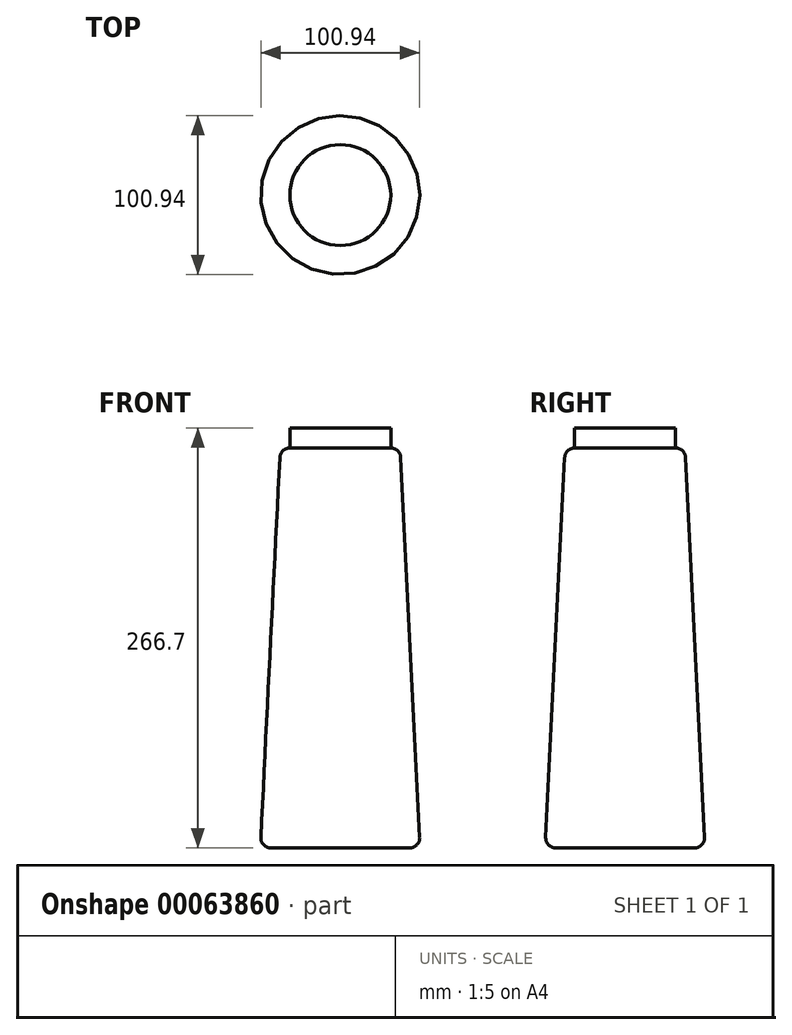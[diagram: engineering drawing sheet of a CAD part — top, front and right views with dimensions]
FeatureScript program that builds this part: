
annotation { "Feature Type Name" : "Feature", "Feature Type Description" : "" }
export const myFeature = defineFeature(function(context is Context, id is Id, definition is map)
    precondition{}
    {
        {
            var Q0;
            Q0=qCreatedBy(makeId("Top.planeOp"),FACE);
            var sketch = newSketch(context, id + "F0", { "sketchPlane" : qUnion([Q0])});
            skCircle(sketch, "E0", {"center": v(0, 0) * mm, "radius": 50.8 * mm});
            skSolve(sketch);
        }
        {
            var Q0;
            Q0=qCreatedBy(makeId("Top.planeOp"),FACE);
            cPlane(context, id + "F1", {"entities" : qUnion([Q0]), "cplaneType" : CPlaneType.OFFSET, "offset" : 254 * mm, "width" : 152.4 * mm, "height" : 152.4 * mm});
        }
        {
            var Q0;
            Q0=qCreatedBy(id+"F1.planeOp",FACE);
            var sketch = newSketch(context, id + "F2", { "sketchPlane" : qUnion([Q0])});
            skCircle(sketch, "E1", {"center": v(0, 0) * mm, "radius": 38.1 * mm});
            skSolve(sketch);
        }
        {
            var Q0;
            Q0=makeQuery(id+"F0.imprint","IMPRINT",FACE,{"disambiguationData":[TD([[makeQuery(id+"F0.imprint","IMPRINT",EDGE,{"derivedFrom":sQuery(id+"F0.wireOp",EDGE,"E0")}),1.0]])]});
            var Q1;
            Q1=makeQuery(id+"F2.imprint","IMPRINT",FACE,{"disambiguationData":[TD([[makeQuery(id+"F2.imprint","IMPRINT",EDGE,{"derivedFrom":sQuery(id+"F2.wireOp",EDGE,"E1")}),1.0]])]});
            loft(context, id + "F3", {"sheetProfilesArray" : [{ "sheetProfileEntities" : qUnion([Q0]) }, { "sheetProfileEntities" : qUnion([Q1]) }]});
        }
        {
            var Q0;
            Q0=makeQuery(id+"F3.opLoft","SWEPT_FACE",FACE,{"disambiguationData":[OSD([sQuery(id+"F0.wireOp",EDGE,"E0"),sQuery(id+"F2.wireOp",EDGE,"E1")])]});
            fillet(context, id + "F4", {"entities" : qUnion([Q0]), "radius" : 6.35 * mm, "tangentPropagation" : true, "allowEdgeOverflow" : false});
        }
        {
            var Q0;
            Q0=makeQuery(id+"F3.opLoft","CAP_FACE",FACE,{"disambiguationData":[OSD([makeQuery(id+"F2.imprint","IMPRINT",FACE,{"disambiguationData":[TD([[makeQuery(id+"F2.imprint","IMPRINT",EDGE,{"derivedFrom":sQuery(id+"F2.wireOp",EDGE,"E1")}),1.0]])]})])],"isStart":true});
            extrude(context, id + "F5", {"entities" : qUnion([Q0]), "operationType" : NewBodyOperationType.ADD, "depth" : 12.7 * mm});
        }
    });
